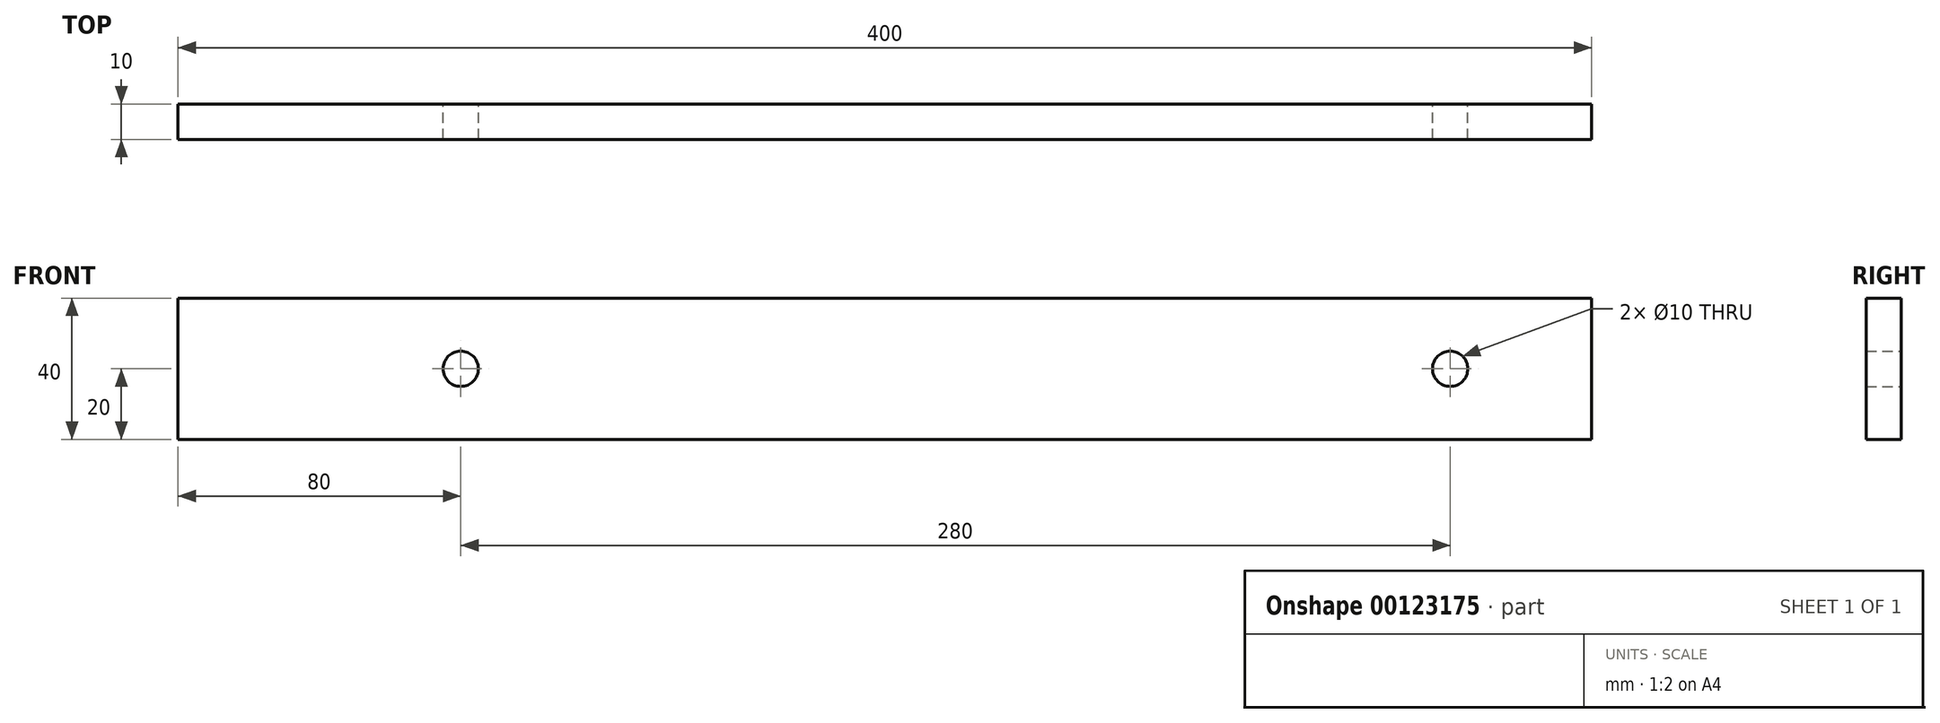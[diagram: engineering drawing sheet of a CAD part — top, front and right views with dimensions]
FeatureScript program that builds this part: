
annotation { "Feature Type Name" : "Feature", "Feature Type Description" : "" }
export const myFeature = defineFeature(function(context is Context, id is Id, definition is map)
    precondition{}
    {
        {
            var Q0;
            Q0=qCreatedBy(makeId("Front.planeOp"),FACE);
            var sketch = newSketch(context, id + "F0", { "sketchPlane" : qUnion([Q0])});
            skLineSegment(sketch, "E0.bottom", {"start": v(200, -20) * mm, "end": v(-200, -20) * mm});
            skLineSegment(sketch, "E0.top", {"start": v(200, 20) * mm, "end": v(-200, 20) * mm});
            skLineSegment(sketch, "E0.left", {"start": v(200, -20) * mm, "end": v(200, 20) * mm});
            skLineSegment(sketch, "E0.right", {"start": v(-200, -20) * mm, "end": v(-200, 20) * mm});
            skPoint(sketch, "E0.middle", {"position": v(0, 0) * mm});
            skCircle(sketch, "E1", {"center": v(-120, 0) * mm, "radius": 5 * mm});
            skCircle(sketch, "E2", {"center": v(160, 0) * mm, "radius": 5 * mm});
            skSolve(sketch);
        }
        {
            var Q0;
            Q0 = qSketchRegion(id + "F0", true);
            extrude(context, id + "F1", {"entities" : qUnion([Q0]), "depth" : 10 * mm});
        }
    });
